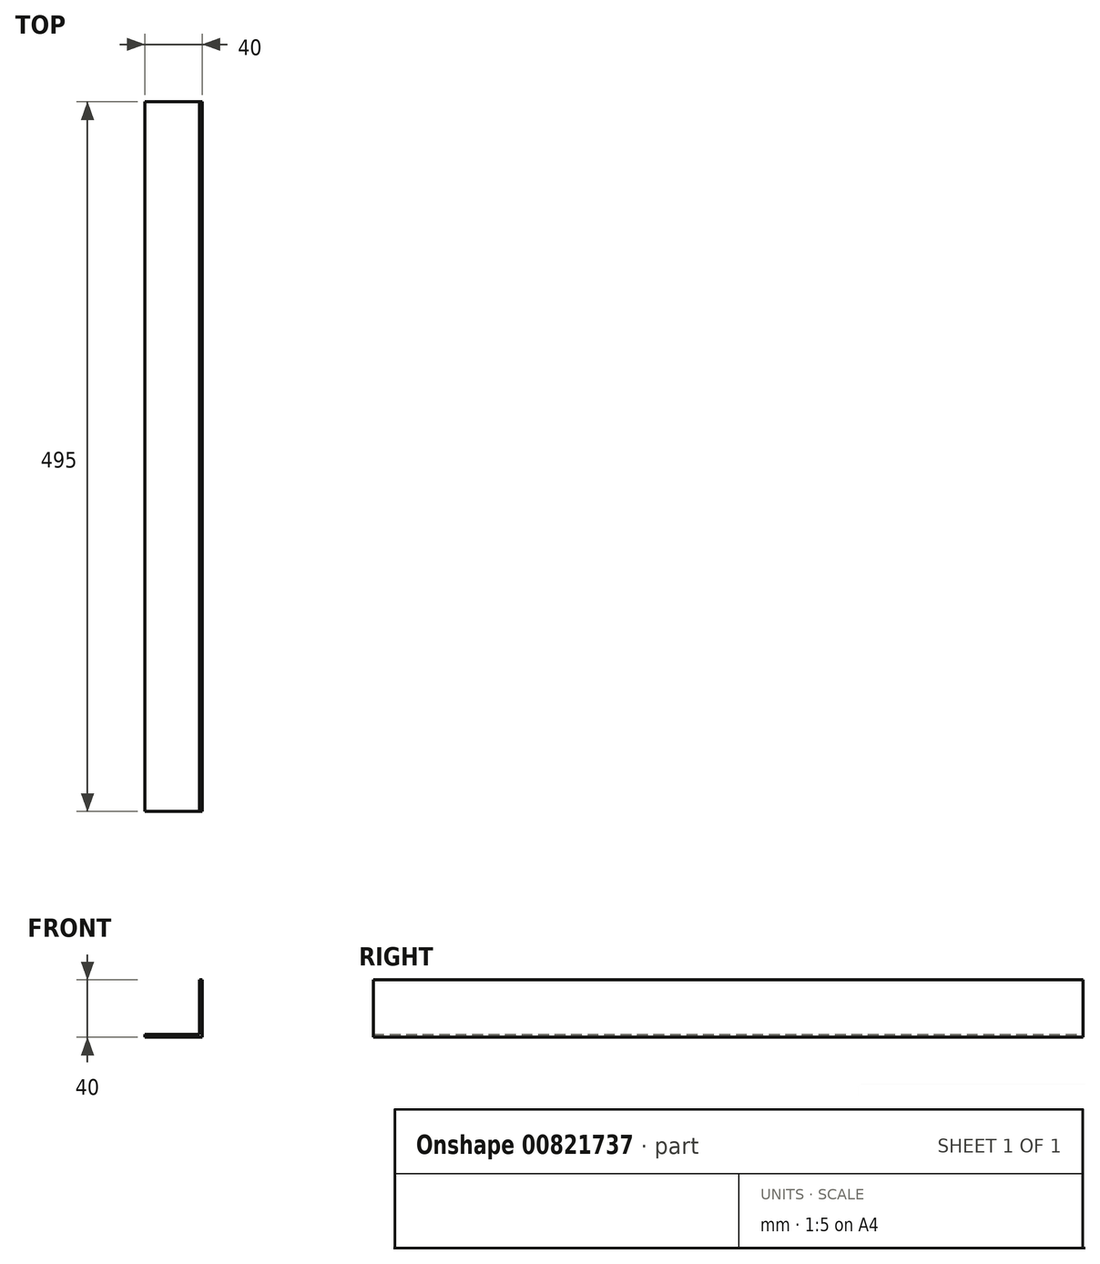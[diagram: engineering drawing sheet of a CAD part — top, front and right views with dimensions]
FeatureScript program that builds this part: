
annotation { "Feature Type Name" : "Feature", "Feature Type Description" : "" }
export const myFeature = defineFeature(function(context is Context, id is Id, definition is map)
    precondition{}
    {
        {
            var Q0;
            Q0=qCreatedBy(makeId("Front.planeOp"),FACE);
            var sketch = newSketch(context, id + "F0", { "sketchPlane" : qUnion([Q0])});
            skLineSegment(sketch, "E0", {"start": v(0, 0) * mm, "end": v(-40, 0) * mm});
            skLineSegment(sketch, "E1", {"start": v(-40, 0) * mm, "end": v(-40, 2) * mm});
            skLineSegment(sketch, "E2", {"start": v(-40, 2) * mm, "end": v(-2, 2) * mm});
            skLineSegment(sketch, "E3", {"start": v(-2, 2) * mm, "end": v(-2, 40) * mm});
            skLineSegment(sketch, "E4", {"start": v(-2, 40) * mm, "end": v(0, 40) * mm});
            skLineSegment(sketch, "E5", {"start": v(0, 40) * mm, "end": v(0, 0) * mm});
            skSolve(sketch);
        }
        {
            var Q0;
            Q0 = qSketchRegion(id + "F0", true);
            extrude(context, id + "F1", {"entities" : qUnion([Q0]), "depth" : 495 * mm, "offsetDistance" : 25 * mm});
        }
    });
